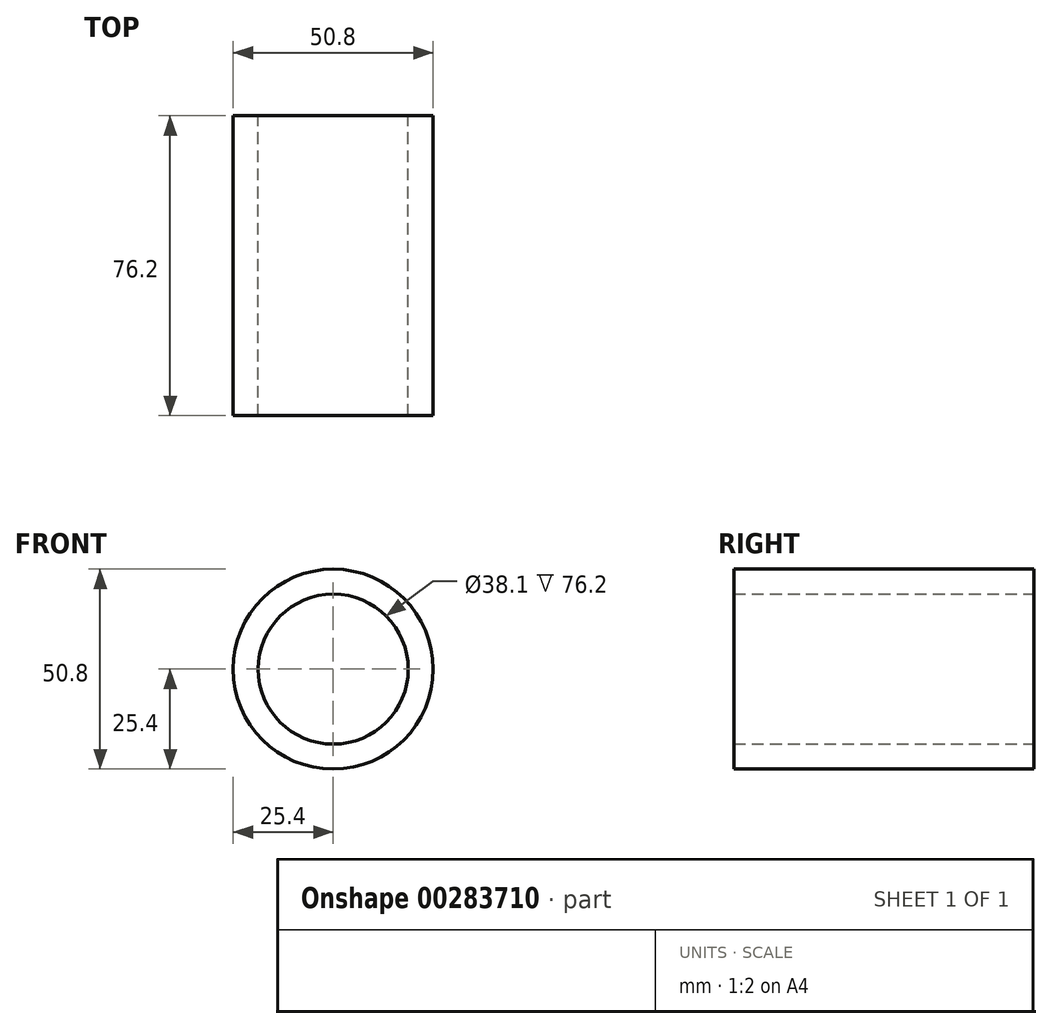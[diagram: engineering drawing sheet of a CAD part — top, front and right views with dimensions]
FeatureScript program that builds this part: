
annotation { "Feature Type Name" : "Feature", "Feature Type Description" : "" }
export const myFeature = defineFeature(function(context is Context, id is Id, definition is map)
    precondition{}
    {
        {
            var Q0;
            Q0=qCreatedBy(makeId("Front.planeOp"),FACE);
            var sketch = newSketch(context, id + "F0", { "sketchPlane" : qUnion([Q0])});
            skCircle(sketch, "E0", {"center": v(0, 0) * mm, "radius": 19.05 * mm});
            skCircle(sketch, "E1.0", {"center": v(0, 0) * mm, "radius": 25.4 * mm});
            skSolve(sketch);
        }
        {
            var Q0;
            Q0=makeQuery(id+"F0.imprint","IMPRINT",FACE,{"disambiguationData":[TD([[makeQuery(id+"F0.imprint","IMPRINT",EDGE,{"derivedFrom":sQuery(id+"F0.wireOp",EDGE,"E0")}),-1.0]])]});
            extrude(context, id + "F1", {"entities" : qUnion([Q0]), "endBound" : BoundingType.SYMMETRIC, "depth" : 76.2 * mm});
        }
    });
